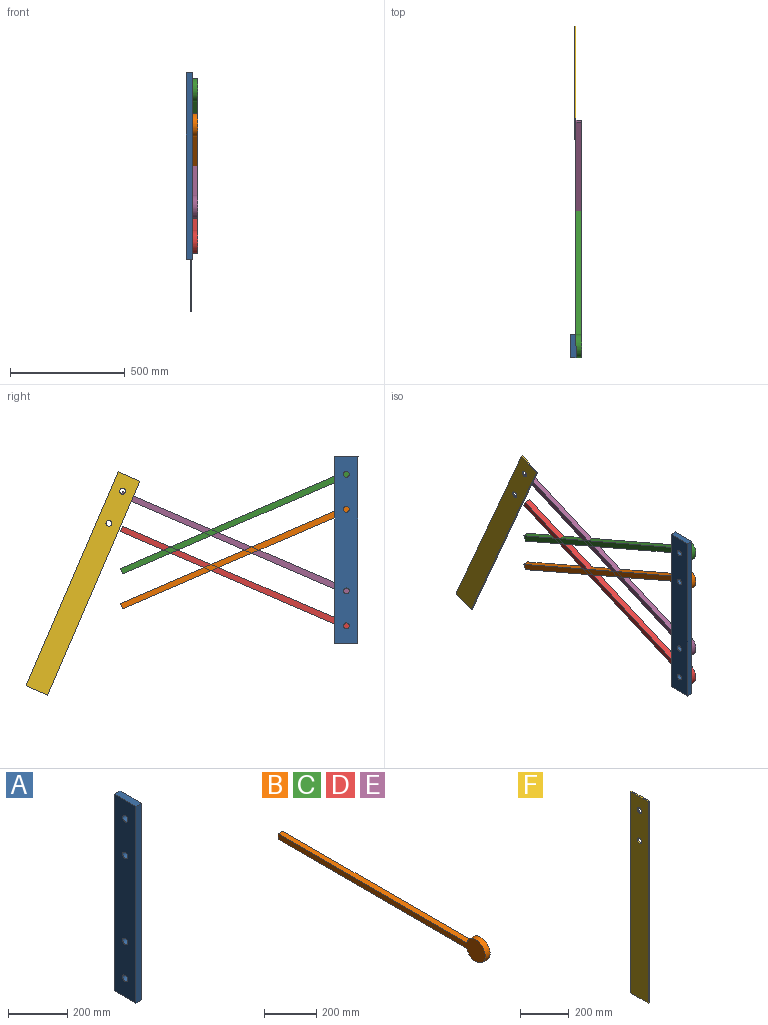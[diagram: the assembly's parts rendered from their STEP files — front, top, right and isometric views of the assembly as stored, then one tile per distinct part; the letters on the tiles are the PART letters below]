
ASSEMBLY  parts=6 mates=5
PART A: 10 faces, bbox 25.4x101.6x812.8 mm
  f0: plane 812.8x25.4mm, normal (0,1,0), area 20645.1mm2, adj f1,f6,f8,f9
  f1: plane 101.6x25.4mm, normal (0,0,1), area 2580.6mm2, adj f0,f2,f8,f9
  f2: plane 812.8x25.4mm, normal (0,-1,0), area 20645.1mm2, adj f1,f6,f8,f9
  f3: cylinder r=12.7mm len=25.4mm, axis (-1,0,0), area 2026.8mm2, adj f8,f9
  f4: cylinder r=12.7mm len=25.4mm, axis (-1,0,0), area 2026.8mm2, adj f8,f9
  f5: cylinder r=12.7mm len=25.4mm, axis (-1,0,0), area 2026.8mm2, adj f8,f9
  f6: plane 101.6x25.4mm, normal (0,0,-1), area 2580.6mm2, adj f0,f2,f8,f9
  f7: cylinder r=12.7mm len=25.4mm, axis (-1,0,0), area 2026.8mm2, adj f8,f9
  f8: plane 812.8x101.6mm, normal (1,0,0), area 80553.7mm2, adj f0,f1,f2,f3,f4,f5,f6,f7
  f9: plane 812.8x101.6mm, normal (-1,0,0), area 80553.7mm2, adj f0,f1,f2,f3,f4,f5,f6,f7
PART B: 6 faces, bbox 25.4x1117.6x101.6 mm
  f0: plane 1017.61x25.4mm, normal (0,0,1), area 25847.4mm2, adj f1,f3,f4,f5
  f1: cylinder r=50.8mm len=101.6mm, axis (-1,0,0), area 7455.2mm2, adj f0,f2,f4,f5
  f2: plane 1017.61x25.4mm, normal (0,0,-1), area 25847.4mm2, adj f1,f3,f4,f5
  f3: plane 25.4x25.4mm, normal (0,1,0), area 645.2mm2, adj f0,f2,f4,f5
  f4: plane 1117.6x101.6mm, normal (1,0,0), area 33927.3mm2, adj f0,f1,f2,f3
  f5: plane 1117.6x101.6mm, normal (-1,0,0), area 33927.3mm2, adj f0,f1,f2,f3
PART C: same geometry as B
PART D: same geometry as B
PART E: same geometry as B
PART F: 8 faces, bbox 6.4x101.6x1016 mm
  f0: plane 1016x6.35mm, normal (0,-1,0), area 6451.6mm2, adj f1,f4,f6,f7
  f1: plane 101.6x6.35mm, normal (0,0,-1), area 645.2mm2, adj f0,f2,f6,f7
  f2: plane 1016x6.35mm, normal (0,1,0), area 6451.6mm2, adj f1,f4,f6,f7
  f3: cylinder r=12.7mm len=25.4mm, axis (-1,0,0), area 506.7mm2, adj f6,f7
  f4: plane 101.6x6.35mm, normal (0,0,1), area 645.2mm2, adj f0,f2,f6,f7
  f5: cylinder r=12.7mm len=25.4mm, axis (-1,0,0), area 506.7mm2, adj f6,f7
  f6: plane 1016x101.6mm, normal (1,0,0), area 102212.2mm2, adj f0,f1,f2,f3,f4,f5
  f7: plane 1016x101.6mm, normal (-1,0,0), area 102212.2mm2, adj f0,f1,f2,f3,f4,f5
PLACE A t=(36.51,107.03,-324.91)mm
PLACE B rot(axis=(-1,0,0),23.3deg) t=(61.91,107.03,-147.11)mm
PLACE C rot(axis=(-1,0,0),23.3deg) t=(61.91,107.03,5.29)mm
PLACE D rot(axis=(1,0,0),23.3deg) t=(61.91,107.03,-655.11)mm
PLACE E rot(axis=(1,0,0),23.3deg) t=(61.91,107.03,-502.71)mm
PLACE F rot(axis=(1,0,0),23.3deg) t=(55.56,1409.74,-957.15)mm
MATE revolute D.f1 <-> A.f5  axis (-1,0,0) through (61.91,107.03,-655.11)mm
MATE revolute F.f5 <-> E.f5  axis (1,0,0) through (61.91,1081.46,-68.32)mm
MATE revolute C.f1 <-> A.f7  axis (-1,0,0) through (61.91,107.03,5.29)mm
MATE revolute E.f1 <-> A.f4  axis (-1,0,0) through (61.91,107.03,-502.71)mm
MATE revolute B.f1 <-> A.f3  axis (-1,0,0) through (61.91,107.03,-147.11)mm
